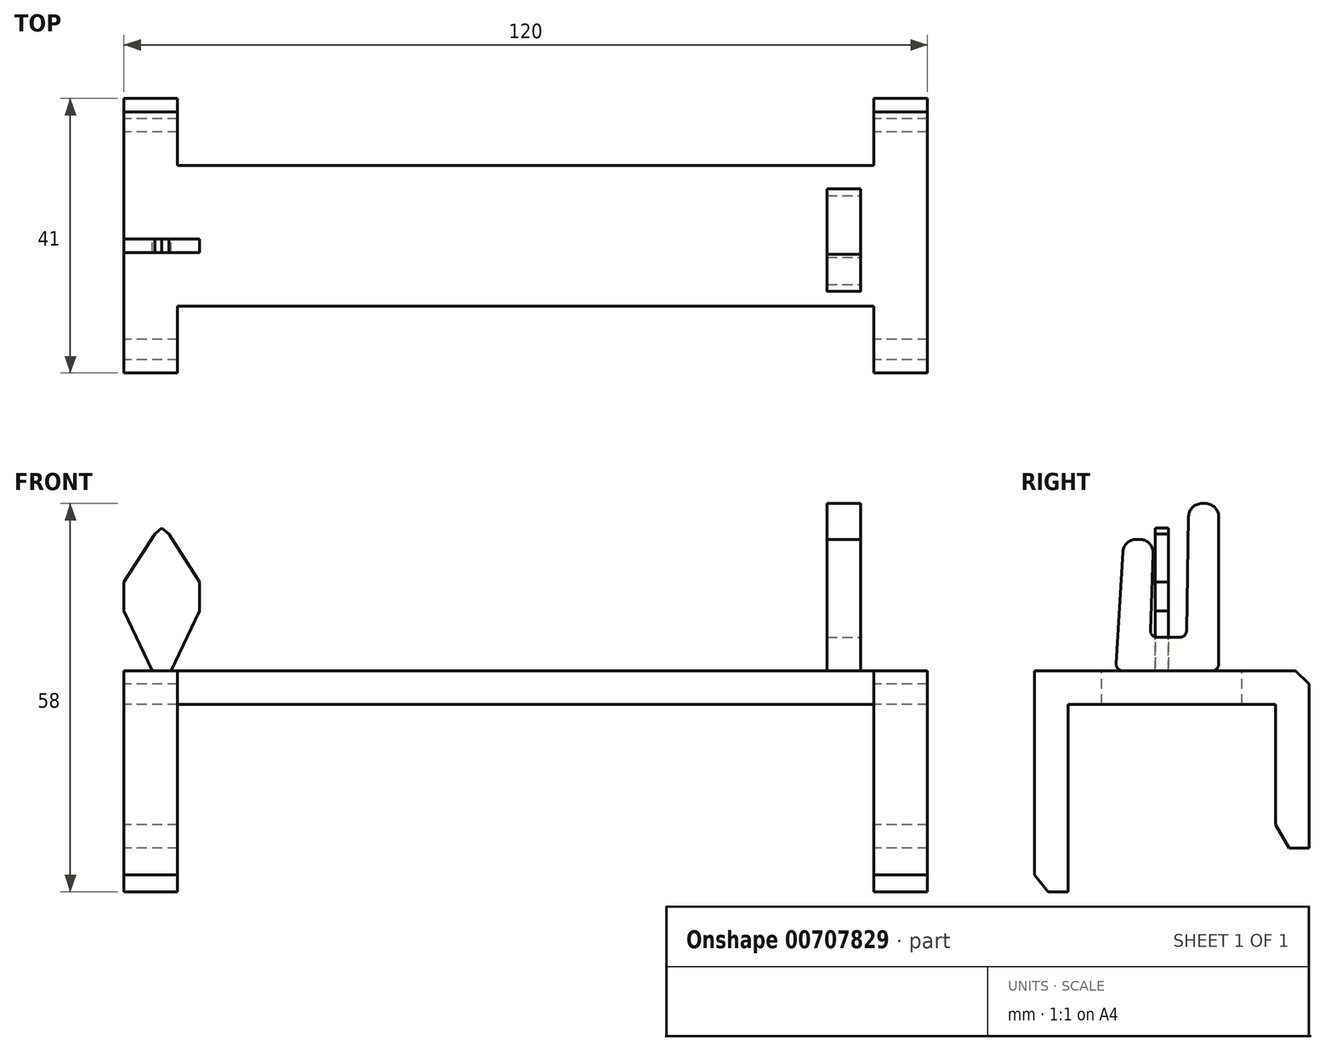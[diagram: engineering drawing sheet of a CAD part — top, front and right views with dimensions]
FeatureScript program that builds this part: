
annotation { "Feature Type Name" : "Feature", "Feature Type Description" : "" }
export const myFeature = defineFeature(function(context is Context, id is Id, definition is map)
    precondition{}
    {
        {
            var Q0;
            Q0=qCreatedBy(makeId("Right.planeOp"),FACE);
            var sketch = newSketch(context, id + "F0", { "sketchPlane" : qUnion([Q0])});
            skLineSegment(sketch, "E0", {"start": v(0, 0) * mm, "end": v(0, -28) * mm});
            skLineSegment(sketch, "E1", {"start": v(0, -28) * mm, "end": v(-3, -28) * mm});
            skLineSegment(sketch, "E2", {"start": v(-3, -28) * mm, "end": v(-5, -25.5) * mm});
            skLineSegment(sketch, "E3", {"start": v(-5, -25.5) * mm, "end": v(-5, 5) * mm});
            skLineSegment(sketch, "E4", {"start": v(-5, 5) * mm, "end": v(34, 5) * mm});
            skLineSegment(sketch, "E5", {"start": v(34, 5) * mm, "end": v(36, 3) * mm});
            skLineSegment(sketch, "E6", {"start": v(36, 3) * mm, "end": v(36, -21.46) * mm});
            skLineSegment(sketch, "E7", {"start": v(0, 0) * mm, "end": v(31, 0) * mm});
            skLineSegment(sketch, "E8", {"start": v(31, 0) * mm, "end": v(31, -18) * mm});
            skLineSegment(sketch, "E9", {"start": v(31, -18) * mm, "end": v(33, -21.46) * mm});
            skLineSegment(sketch, "E10", {"start": v(33, -21.46) * mm, "end": v(36, -21.46) * mm});
            skSolve(sketch);
        }
        {
            var Q0;
            Q0 = qSketchRegion(id + "F0", true);
            extrude(context, id + "F1", {"entities" : qUnion([Q0]), "endBound" : BoundingType.SYMMETRIC, "depth" : 120 * mm, "offsetDistance" : 25 * mm});
        }
        {
            var Q0;
            Q0=makeQuery(id+"F1.opExtrude","SWEPT_FACE",FACE,{"disambiguationData":[OSD([sQuery(id+"F0.wireOp",EDGE,"E3")])]});
            var sketch = newSketch(context, id + "F2", { "sketchPlane" : qUnion([Q0])});
            skLineSegment(sketch, "E11.bottom", {"start": v(52, -28) * mm, "end": v(-52, -28) * mm});
            skLineSegment(sketch, "E11.top", {"start": v(52, 5) * mm, "end": v(-52, 5) * mm});
            skLineSegment(sketch, "E11.left", {"start": v(52, -28) * mm, "end": v(52, 5) * mm});
            skLineSegment(sketch, "E11.right", {"start": v(-52, -28) * mm, "end": v(-52, 5) * mm});
            skSolve(sketch);
        }
        {
            var Q0;
            Q0 = qSketchRegion(id + "F2", true);
            extrude(context, id + "F3", {"entities" : qUnion([Q0]), "operationType" : NewBodyOperationType.REMOVE, "oppositeDirection" : true, "depth" : 10 * mm, "offsetDistance" : 25 * mm});
        }
        {
            var Q0;
            Q0=makeQuery(id+"F1.opExtrude","SWEPT_FACE",FACE,{"disambiguationData":[OSD([sQuery(id+"F0.wireOp",EDGE,"E6")])]});
            var sketch = newSketch(context, id + "F4", { "sketchPlane" : qUnion([Q0])});
            skLineSegment(sketch, "E12.bottom", {"start": v(52, -21.46) * mm, "end": v(-52, -21.46) * mm});
            skLineSegment(sketch, "E12.top", {"start": v(52, 5) * mm, "end": v(-52, 5) * mm});
            skLineSegment(sketch, "E12.left", {"start": v(52, -21.46) * mm, "end": v(52, 5) * mm});
            skLineSegment(sketch, "E12.right", {"start": v(-52, -21.46) * mm, "end": v(-52, 5) * mm});
            skSolve(sketch);
        }
        {
            var Q0;
            Q0 = qSketchRegion(id + "F4", true);
            extrude(context, id + "F5", {"entities" : qUnion([Q0]), "operationType" : NewBodyOperationType.REMOVE, "oppositeDirection" : true, "depth" : 10 * mm, "offsetDistance" : 25 * mm});
        }
        {
            var Q0;
            Q0=qCreatedBy(makeId("Right.planeOp"),FACE);
            cPlane(context, id + "F6", {"entities" : qUnion([Q0]), "cplaneType" : CPlaneType.OFFSET, "offset" : 50 * mm, "width" : 150 * mm, "height" : 150 * mm});
        }
        {
            var Q0;
            Q0=qCreatedBy(id+"F6.planeOp",FACE);
            var sketch = newSketch(context, id + "F7", { "sketchPlane" : qUnion([Q0])});
            skLineSegment(sketch, "E13", {"start": v(17.5, 5) * mm, "end": v(21.5, 5) * mm});
            skLineSegment(sketch, "E14", {"start": v(22.5, 6) * mm, "end": v(22.5, 28) * mm});
            skLineSegment(sketch, "E15", {"start": v(20.5, 30) * mm, "end": v(20, 30) * mm});
            skLineSegment(sketch, "E16", {"start": v(18, 28.04) * mm, "end": v(17.7, 10.98) * mm});
            skLineSegment(sketch, "E17", {"start": v(16.7, 10) * mm, "end": v(13.3, 10) * mm});
            skLineSegment(sketch, "E18", {"start": v(12.3, 11.03) * mm, "end": v(12.7, 22.58) * mm});
            skLineSegment(sketch, "E19", {"start": v(10.7, 24.64) * mm, "end": v(10.2, 24.64) * mm});
            skLineSegment(sketch, "E20", {"start": v(8.2, 22.77) * mm, "end": v(7.2, 6.06) * mm});
            skLineSegment(sketch, "E21", {"start": v(8.19, 5) * mm, "end": v(12.5, 5) * mm});
            skLineSegment(sketch, "E22", {"start": v(12.6, 0) * mm, "end": v(17.4, 0) * mm});
            skLineSegment(sketch, "E23", {"start": v(17.4, 0) * mm, "end": v(17.5, 5) * mm});
            skPoint(sketch, "E24.visualSharp", {"position": v(8.31, 24.64) * mm});
            skArc(sketch, "E24.filletArc", {"start": v(10.2, 24.64) * mm, "mid": v(8.83, 24.1) * mm, "end": v(8.2, 22.77) * mm});
            skPoint(sketch, "E25.visualSharp", {"position": v(12.77, 24.64) * mm});
            skArc(sketch, "E25.filletArc", {"start": v(12.7, 22.58) * mm, "mid": v(12.14, 24.03) * mm, "end": v(10.7, 24.64) * mm});
            skPoint(sketch, "E26.visualSharp", {"position": v(18.03, 30) * mm});
            skArc(sketch, "E26.filletArc", {"start": v(20, 30) * mm, "mid": v(18.6, 29.43) * mm, "end": v(18, 28.04) * mm});
            skPoint(sketch, "E27.visualSharp", {"position": v(22.5, 30) * mm});
            skArc(sketch, "E27.filletArc", {"start": v(22.5, 28) * mm, "mid": v(21.91, 29.41) * mm, "end": v(20.5, 30) * mm});
            skPoint(sketch, "E28.visualSharp", {"position": v(12.26, 10) * mm});
            skArc(sketch, "E28.filletArc", {"start": v(12.3, 11.03) * mm, "mid": v(12.58, 10.3) * mm, "end": v(13.3, 10) * mm});
            skPoint(sketch, "E29.visualSharp", {"position": v(17.68, 10) * mm});
            skArc(sketch, "E29.filletArc", {"start": v(16.7, 10) * mm, "mid": v(17.4, 10.29) * mm, "end": v(17.7, 10.98) * mm});
            skPoint(sketch, "E30.visualSharp", {"position": v(7.13, 5) * mm});
            skArc(sketch, "E30.filletArc", {"start": v(7.2, 6.06) * mm, "mid": v(7.46, 5.31) * mm, "end": v(8.19, 5) * mm});
            skPoint(sketch, "E31.visualSharp", {"position": v(22.5, 5) * mm});
            skArc(sketch, "E31.filletArc", {"start": v(21.5, 5) * mm, "mid": v(22.2, 5.3) * mm, "end": v(22.5, 6) * mm});
            skLineSegment(sketch, "E32", {"start": v(15, 0) * mm, "end": v(15, 10) * mm, "construction": true});
            skLineSegment(sketch, "E33", {"start": v(12.5, 5) * mm, "end": v(12.6, 0) * mm});
            skSolve(sketch);
        }
        {
            var Q0;
            Q0 = qSketchRegion(id + "F7", true);
            extrude(context, id + "F8", {"entities" : qUnion([Q0]), "operationType" : NewBodyOperationType.ADD, "oppositeDirection" : true, "depth" : 5 * mm, "offsetDistance" : 25 * mm});
        }
        {
            var Q0;
            Q0=qCreatedBy(makeId("Front.planeOp"),FACE);
            cPlane(context, id + "F9", {"entities" : qUnion([Q0]), "cplaneType" : CPlaneType.OFFSET, "offset" : 15 * mm, "oppositeDirection" : true, "width" : 150 * mm, "height" : 150 * mm});
        }
        {
            var Q0;
            Q0=qCreatedBy(id+"F9.planeOp",FACE);
            var sketch = newSketch(context, id + "F10", { "sketchPlane" : qUnion([Q0])});
            skLineSegment(sketch, "E34", {"start": v(-60, 18.27) * mm, "end": v(-60, 13.93) * mm});
            skLineSegment(sketch, "E35", {"start": v(-60, 13.93) * mm, "end": v(-55.75, 5) * mm});
            skLineSegment(sketch, "E36", {"start": v(-55.75, 5) * mm, "end": v(-53, 5) * mm});
            skLineSegment(sketch, "E37", {"start": v(-53, 5) * mm, "end": v(-48.74, 13.93) * mm});
            skLineSegment(sketch, "E38", {"start": v(-48.74, 13.93) * mm, "end": v(-48.74, 18.27) * mm});
            skLineSegment(sketch, "E39", {"start": v(-48.74, 18.27) * mm, "end": v(-60, 18.27) * mm});
            skLineSegment(sketch, "E40", {"start": v(-54.37, 5) * mm, "end": v(-54.37, 26.54) * mm, "construction": true});
            skPoint(sketch, "E40.endSnap0", {"position": v(-54.37, 18.27) * mm});
            skLineSegment(sketch, "E41", {"start": v(-60, 18.27) * mm, "end": v(-55.41, 25.41) * mm});
            skLineSegment(sketch, "E42", {"start": v(-55.41, 25.41) * mm, "end": v(-54.37, 26.31) * mm});
            skLineSegment(sketch, "E43", {"start": v(-54.37, 26.31) * mm, "end": v(-53.33, 25.41) * mm});
            skLineSegment(sketch, "E44", {"start": v(-53.33, 25.41) * mm, "end": v(-48.74, 18.27) * mm});
            skSolve(sketch);
        }
        {
            var Q0;
            Q0 = qSketchRegion(id + "F10", true);
            extrude(context, id + "F11", {"entities" : qUnion([Q0]), "operationType" : NewBodyOperationType.ADD, "depth" : 2 * mm, "offsetDistance" : 25 * mm});
        }
    });
